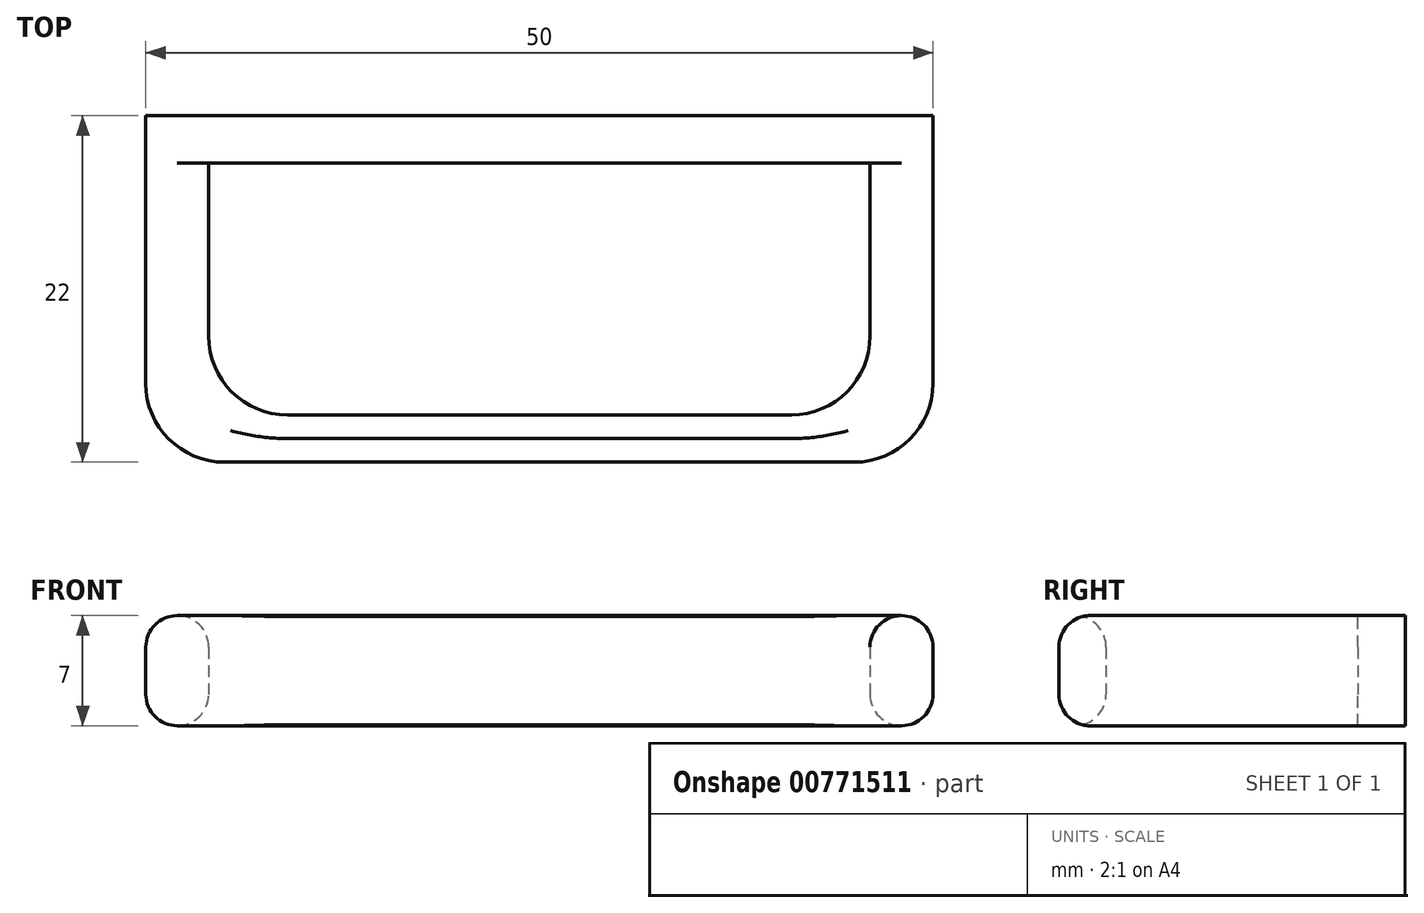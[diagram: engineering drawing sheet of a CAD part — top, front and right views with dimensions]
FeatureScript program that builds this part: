
annotation { "Feature Type Name" : "Feature", "Feature Type Description" : "" }
export const myFeature = defineFeature(function(context is Context, id is Id, definition is map)
    precondition{}
    {
        {
            var Q0;
            Q0=qCreatedBy(makeId("Top.planeOp"),FACE);
            var sketch = newSketch(context, id + "F0", { "sketchPlane" : qUnion([Q0])});
            skLineSegment(sketch, "E0.bottom", {"start": v(-54.45, -29) * mm, "end": v(-4.45, -29) * mm});
            skLineSegment(sketch, "E0.top", {"start": v(-49.45, -51) * mm, "end": v(-9.45, -51) * mm});
            skLineSegment(sketch, "E0.left", {"start": v(-54.45, -29) * mm, "end": v(-54.45, -46) * mm});
            skLineSegment(sketch, "E0.right", {"start": v(-4.45, -29) * mm, "end": v(-4.45, -46) * mm});
            skPoint(sketch, "E1.visualSharp", {"position": v(-4.45, -51) * mm});
            skArc(sketch, "E1.filletArc", {"start": v(-9.45, -51) * mm, "mid": v(-5.92, -49.53) * mm, "end": v(-4.45, -46) * mm});
            skPoint(sketch, "E2.visualSharp", {"position": v(-14.45, -43.55) * mm});
            skPoint(sketch, "E3.visualSharp", {"position": v(-47.45, -41) * mm});
            skPoint(sketch, "E4.visualSharp", {"position": v(-54.45, -51) * mm});
            skArc(sketch, "E4.filletArc", {"start": v(-54.45, -46) * mm, "mid": v(-52.99, -49.53) * mm, "end": v(-49.45, -51) * mm});
            skLineSegment(sketch, "E5.bottom", {"start": v(-50.45, -32) * mm, "end": v(-8.45, -32) * mm});
            skLineSegment(sketch, "E5.top", {"start": v(-45.45, -48) * mm, "end": v(-13.45, -48) * mm});
            skLineSegment(sketch, "E5.left", {"start": v(-50.45, -32) * mm, "end": v(-50.45, -43) * mm});
            skLineSegment(sketch, "E5.right", {"start": v(-8.45, -32) * mm, "end": v(-8.45, -43) * mm});
            skPoint(sketch, "E6.visualSharp", {"position": v(-50.45, -48) * mm});
            skArc(sketch, "E6.filletArc", {"start": v(-50.45, -43) * mm, "mid": v(-48.99, -46.53) * mm, "end": v(-45.45, -48) * mm});
            skPoint(sketch, "E7.visualSharp", {"position": v(-8.45, -48) * mm});
            skArc(sketch, "E7.filletArc", {"start": v(-13.45, -48) * mm, "mid": v(-9.92, -46.53) * mm, "end": v(-8.45, -43) * mm});
            skSolve(sketch);
        }
        {
            var Q0;
            Q0=makeQuery(id+"F0.imprint","IMPRINT",FACE,{"disambiguationData":[TD([[makeQuery(id+"F0.imprint","IMPRINT",EDGE,{"derivedFrom":sQuery(id+"F0.wireOp",EDGE,"E0.bottom")}),-1.0]])]});
            extrude(context, id + "F1", {"entities" : qUnion([Q0]), "depth" : 7 * mm, "offsetDistance" : 25 * mm});
        }
        {
            var Q0;
            Q0=makeQuery(id+"F1.opExtrude","CAP_EDGE",EDGE,{"disambiguationData":[OSD([sQuery(id+"F0.wireOp",EDGE,"E5.top")])],"isStart":false});
            var Q1;
            Q1=makeQuery(id+"F1.opExtrude","CAP_EDGE",EDGE,{"disambiguationData":[OSD([sQuery(id+"F0.wireOp",EDGE,"E0.top")])],"isStart":false});
            var Q2;
            Q2=makeQuery(id+"F1.opExtrude","CAP_EDGE",EDGE,{"disambiguationData":[OSD([sQuery(id+"F0.wireOp",EDGE,"E0.left")])],"isStart":true});
            var Q3;
            Q3=makeQuery(id+"F1.opExtrude","CAP_EDGE",EDGE,{"disambiguationData":[OSD([sQuery(id+"F0.wireOp",EDGE,"E5.top")])],"isStart":true});
            fillet(context, id + "F2", {"entities" : qUnion([Q0, Q1, Q2, Q3]), "radius" : 2 * mm, "tangentPropagation" : true, "allowEdgeOverflow" : false});
        }
    });
